# Revit family: Lighting_Outside_Focus-Lighting_Peak-320----1
name_source: partatom
category: Lighting Fixtures
units: mm (PartAtom-declared; Revit-internal decimal feet)

## family parameters
Cut with Voids When Loaded = No
Host = Face
Light Source = No
Maintain Annotation Orientation = No
OmniClass Number = 23.80.70.14
OmniClass Title = Luminaries for External Lighting
Part Type = Normal
Room Calculation Point = No
Round Connector Dimension = Use Diameter
Shared = No

## types (3) — shared parameters
Apparent Load = 0 VA
Default Elevation = 1219 mm
Description = Peak 320 is available in two different versions for vertical pole and horizontal arm, respectively. The same strong and characteristic design with optimized and simplified adaptions for pole/arm.
Height = 119 mm  [stored 0.39042 ft]
Installation Type = Side Entry or Post Top
Lamp = LED
Lens Material = Focus-Lighting - Acrylic - LED
Manufacturer = Focus-Lighting
Model = Peak 320
Number of Poles = 1
Photometric Option Note = Please select the appropriate type from the drop-down list above.
Power Factor = 1
Product Material = Focus-Lighting - Metal - Cast Aluminium
Product data url = https://www.bimobject.com
URL = https://www.focus-lighting.dk
Version = 1
Voltage = 230 V
Watts = 0 W
Weight - Mass = 7.00 kg
Width = 208 mm  [stored 0.682415 ft]

## per-type parameters (varying)
| type | Photometric Option |
| Peak 320 - 2700K | Peak 320 : Peak 320 - 2700K |
| Peak 320 - 3000K | Peak 320 : Peak 320 - 3000K |
| Peak 320 - 4000K | Peak 320 : Peak 320 - 4000K |

note: [stored X ft] marks values corroborated as IEEE doubles in the binary element streams (Revit-internal decimal feet)

## geometry (parser evidence)
native form markers: Sweep x5
no freeform markers — native parametric forms only
